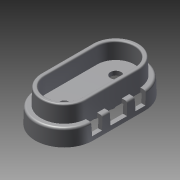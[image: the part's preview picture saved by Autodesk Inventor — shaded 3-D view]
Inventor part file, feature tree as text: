
AUTODESK INVENTOR PART (.ipt)
format: ipt  version: 2013 (Build 170138000, 138)  size: 235,520 bytes
history: native  units: in
note: dims shown in document units (in); Inventor stores cm internally (conversion verified against a paired STEP export)
features: extrude x8, sketch x6, plane x3, fillet x2
ambient origin geometry x8: Origin, YZ Plane, XZ Plane, XY Plane, X Axis, Y Axis, Z Axis, Center Point
bodies: Solid1 (feature_tree)
feature tree (19):
  sketch  "Sketch1"  dims[d0=0.157in d1=-0.0103in d2=0.118in d3=-0.0034in]
  extrude  "Extrusion1"  Depth=0.118in
  extrude  "Extrusion2"  [1 undecoded]
  extrude  "Extrusion3"  Depth=1.0in TaperAngle=0.0deg
  plane  "Work Plane1"
  sketch  "Sketch3"  dims[d7=0.125in d8=0.0in d9=1.0in d10=0.0in]
  extrude  "Extrusion4"  TaperAngle=0.0deg  [1 undecoded]
  extrude  "Extrusion5"  TaperAngle=0.0deg  [1 undecoded]
  extrude  "Extrusion6"  Depth=0.02in
  plane  "Work Plane2"
  extrude  "Extrusion7"  Depth=0.012in
  plane  "Work Plane3"
  extrude  "Extrusion8"  [1 undecoded]
  fillet  "Fillet1"  [1 undecoded]
  fillet  "Fillet2"  [1 undecoded]
  sketch  "Sketch2"  dims[d4=0.157in d5=-0.0103in d6=-0.157in]
  sketch  "Sketch4"  dims[d11=0.079in d12=0.0in d13=0.0in]
  sketch  "Sketch5"  dims[d14=1.0in d15=0.0in d16=0.0in]
  sketch  "Sketch6"  dims[d17=1.0in d18=0.0in d19=0.02in d20=0.012in]
note: 6 required parameter values undecoded (feature->parameter linkage not recoverable at this tier; creation-order binding heuristic only, values carry confidence <= 0.55)
